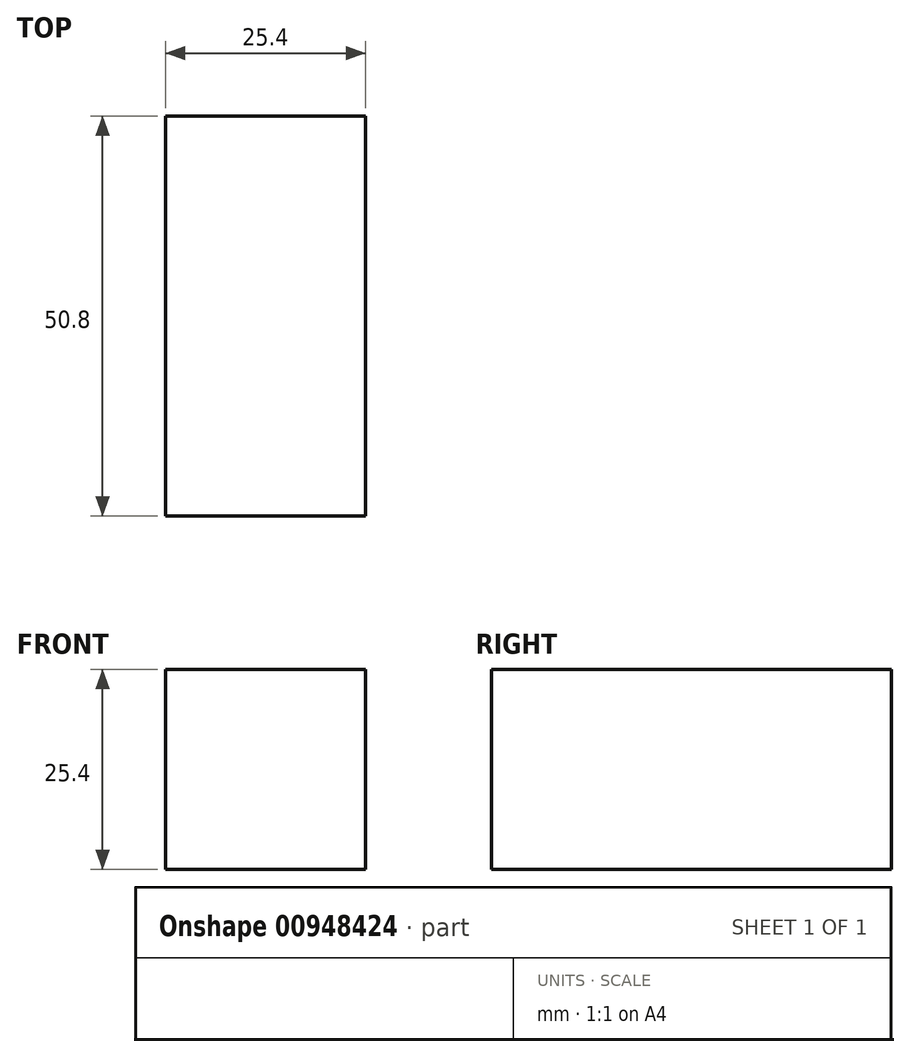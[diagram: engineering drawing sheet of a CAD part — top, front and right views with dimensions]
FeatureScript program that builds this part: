
annotation { "Feature Type Name" : "Feature", "Feature Type Description" : "" }
export const myFeature = defineFeature(function(context is Context, id is Id, definition is map)
    precondition{}
    {
        {
            var Q0;
            Q0=qCreatedBy(makeId("Front.planeOp"),FACE);
            var sketch = newSketch(context, id + "F0", { "sketchPlane" : qUnion([Q0])});
            skLineSegment(sketch, "E0.bottom", {"start": v(10.08, 3.13) * mm, "end": v(35.48, 3.13) * mm});
            skLineSegment(sketch, "E0.top", {"start": v(10.08, -22.27) * mm, "end": v(35.48, -22.27) * mm});
            skLineSegment(sketch, "E0.left", {"start": v(10.08, 3.13) * mm, "end": v(10.08, -22.27) * mm});
            skLineSegment(sketch, "E0.right", {"start": v(35.48, 3.13) * mm, "end": v(35.48, -22.27) * mm});
            skSolve(sketch);
        }
        {
            var Q0;
            Q0=makeQuery(id+"F0.imprint","IMPRINT",FACE,{"disambiguationData":[TD([[makeQuery(id+"F0.imprint","IMPRINT",EDGE,{"derivedFrom":sQuery(id+"F0.wireOp",EDGE,"E0.bottom")}),-1.0]])]});
            extrude(context, id + "F1", {"entities" : qUnion([Q0]), "depth" : 25.4 * mm, "offsetDistance" : 25.4 * mm});
        }
        {
            var Q0;
            Q0=qCreatedBy(makeId("Front.planeOp"),FACE);
            var sketch = newSketch(context, id + "F2", { "sketchPlane" : qUnion([Q0])});
            skCircle(sketch, "E1", {"center": v(20.08, -9.16) * mm, "radius": 6.35 * mm});
            skSolve(sketch);
        }
        {
            var Q0;
            Q0 = qSketchRegion(id + "F2", true);
            extrude(context, id + "F3", {"entities" : qUnion([Q0]), "operationType" : NewBodyOperationType.ADD, "depth" : 25.4 * mm, "offsetDistance" : 25.4 * mm});
        }
        {
            var Q0;
            Q0=makeQuery(id+"F1.opExtrude","CAP_FACE",FACE,{"disambiguationData":[OSD([sQuery(id+"F0.wireOp",EDGE,"E0.bottom"),sQuery(id+"F0.wireOp",EDGE,"E0.top"),sQuery(id+"F0.wireOp",EDGE,"E0.left"),sQuery(id+"F0.wireOp",EDGE,"E0.right")])],"isStart":false});
            var sketch = newSketch(context, id + "F4", { "sketchPlane" : qUnion([Q0])});
            skSolve(sketch);
        }
        {
            var Q0;
            Q0=makeQuery(id+"F4.imprint","IMPRINT",FACE,{"disambiguationData":[TD([[makeQuery(id+"F4.imprint","IMPRINT",EDGE,{"derivedFrom":makeQuery(id+"F1.opExtrude","CAP_EDGE",EDGE,{"disambiguationData":[OSD([sQuery(id+"F0.wireOp",EDGE,"E0.bottom")])],"isStart":false})}),-1.0]])]});
            extrude(context, id + "F5", {"entities" : qUnion([Q0]), "operationType" : NewBodyOperationType.ADD, "depth" : 25.4 * mm, "offsetDistance" : 25.4 * mm});
        }
    });
